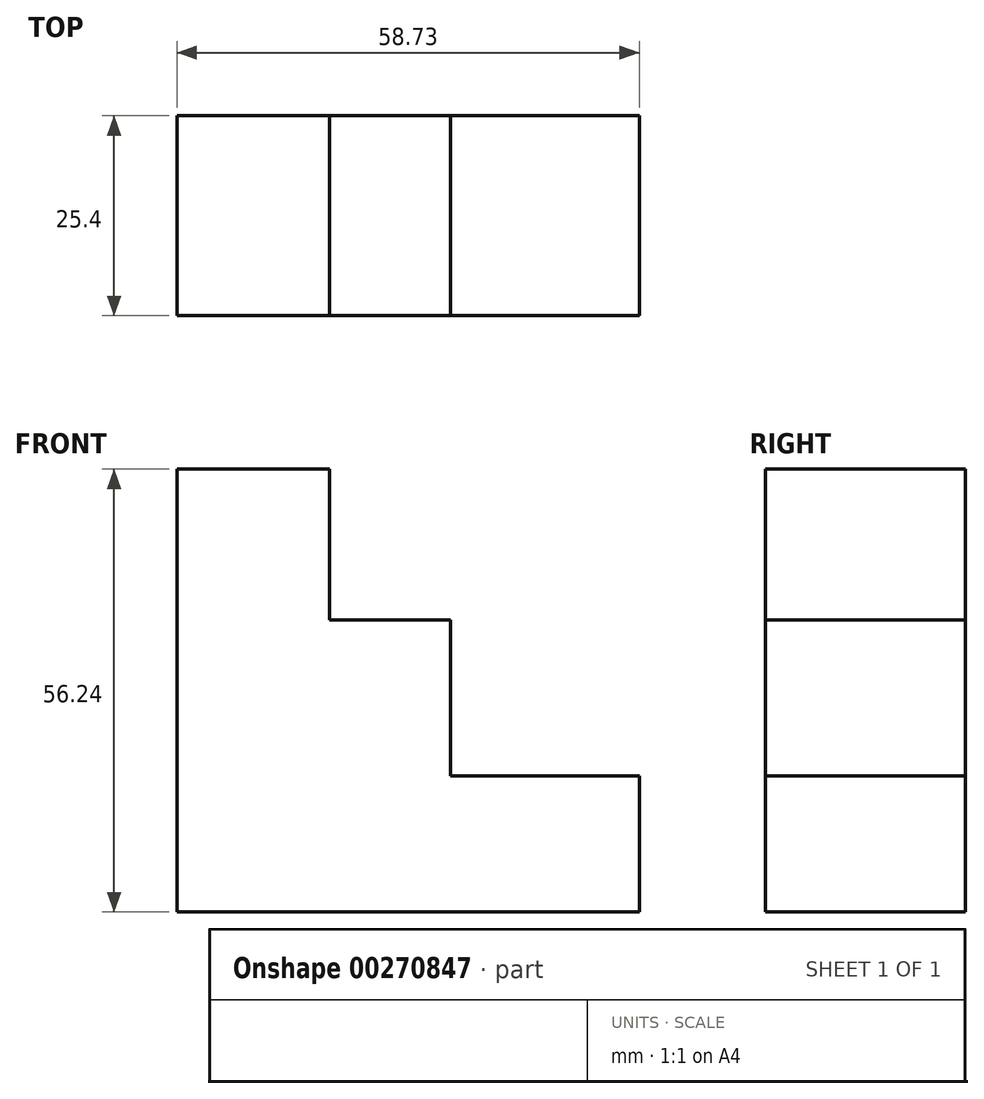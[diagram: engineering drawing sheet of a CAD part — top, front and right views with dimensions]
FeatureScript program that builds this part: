
annotation { "Feature Type Name" : "Feature", "Feature Type Description" : "" }
export const myFeature = defineFeature(function(context is Context, id is Id, definition is map)
    precondition{}
    {
        {
            var Q0;
            Q0=qCreatedBy(makeId("Front.planeOp"),FACE);
            var sketch = newSketch(context, id + "F0", { "sketchPlane" : qUnion([Q0])});
            skLineSegment(sketch, "E0", {"start": v(0, 0) * mm, "end": v(-58.73, 0) * mm});
            skLineSegment(sketch, "E1", {"start": v(-58.73, 0) * mm, "end": v(-58.73, 56.24) * mm});
            skLineSegment(sketch, "E2", {"start": v(-58.73, 56.24) * mm, "end": v(-39.36, 56.24) * mm});
            skLineSegment(sketch, "E3", {"start": v(-39.36, 56.24) * mm, "end": v(-39.36, 37.06) * mm});
            skLineSegment(sketch, "E4", {"start": v(-39.36, 37.06) * mm, "end": v(-23.97, 37.06) * mm});
            skLineSegment(sketch, "E5", {"start": v(-23.97, 37.06) * mm, "end": v(-23.97, 17.28) * mm});
            skLineSegment(sketch, "E6", {"start": v(-23.97, 17.28) * mm, "end": v(0, 17.28) * mm});
            skLineSegment(sketch, "E7", {"start": v(0, 17.28) * mm, "end": v(0, 0) * mm});
            skSolve(sketch);
        }
        {
            var Q0;
            Q0 = qSketchRegion(id + "F0", true);
            extrude(context, id + "F1", {"entities" : qUnion([Q0]), "depth" : 25.4 * mm});
        }
    });
